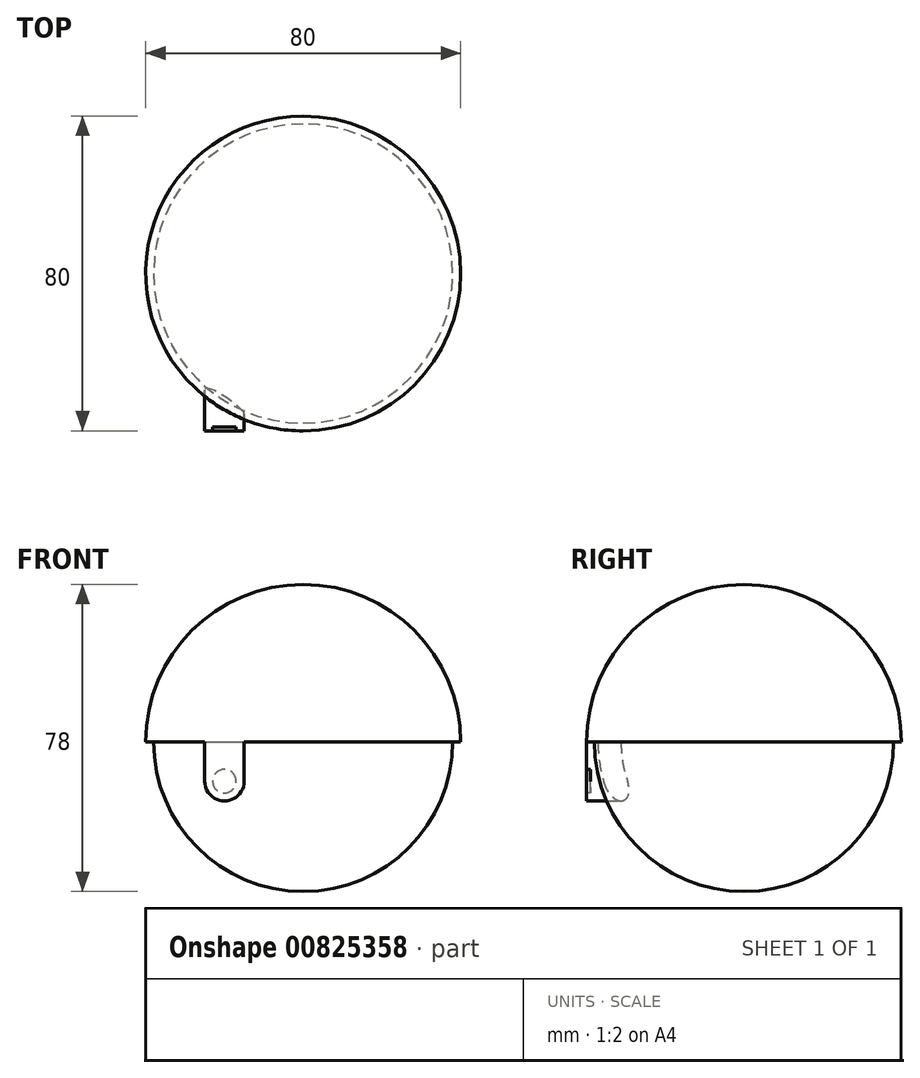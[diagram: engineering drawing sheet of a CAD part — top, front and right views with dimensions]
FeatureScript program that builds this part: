
annotation { "Feature Type Name" : "Feature", "Feature Type Description" : "" }
export const myFeature = defineFeature(function(context is Context, id is Id, definition is map)
    precondition{}
    {
        {
            var Q0;
            Q0=qCreatedBy(makeId("Top.planeOp"),FACE);
            var sketch = newSketch(context, id + "F0", { "sketchPlane" : qUnion([Q0])});
            skArc(sketch, "E0", {"start": v(0, 40) * mm, "mid": v(-40, 0) * mm, "end": v(0, -40) * mm});
            skLineSegment(sketch, "E1", {"start": v(0, 40) * mm, "end": v(0, -40) * mm});
            skSolve(sketch);
        }
        {
            var Q0;
            Q0=makeQuery(id+"F0.imprint","IMPRINT",FACE,{"disambiguationData":[TD([[makeQuery(id+"F0.imprint","IMPRINT",EDGE,{"derivedFrom":sQuery(id+"F0.wireOp",EDGE,"E0")}),1.0]])]});
            var Q1;
            Q1=sQuery(id+"F0.wireOp",EDGE,"E1");
            revolve(context, id + "F1", {"surfaceOperationType" : NewSurfaceOperationType.NEW, "entities" : qUnion([Q0]), "axis" : qUnion([Q1]), "revolveType" : RevolveType.ONE_DIRECTION, "angle" : 180 * degree});
        }
        {
            var Q0;
            Q0=qCreatedBy(makeId("Front.planeOp"),FACE);
            var sketch = newSketch(context, id + "F2", { "sketchPlane" : qUnion([Q0])});
            skArc(sketch, "E2", {"start": v(-25, -10) * mm, "mid": v(-20, -15) * mm, "end": v(-15, -10) * mm});
            skPoint(sketch, "E3.bottom.end.orphan", {"position": v(-15, -5) * mm});
            skPoint(sketch, "E3.bottom.start.orphan", {"position": v(-25, 0) * mm});
            skLineSegment(sketch, "E4", {"start": v(-25, -10) * mm, "end": v(-25, 0) * mm});
            skLineSegment(sketch, "E5", {"start": v(-15, -10) * mm, "end": v(-15, 0) * mm});
            skLineSegment(sketch, "E6", {"start": v(-25, 0) * mm, "end": v(-15, 0) * mm});
            skSolve(sketch);
        }
        {
            var Q0;
            Q0 = qSketchRegion(id + "F2", true);
            extrude(context, id + "F3", {"entities" : qUnion([Q0]), "operationType" : NewBodyOperationType.ADD, "depth" : 40 * mm, "offsetDistance" : 25 * mm});
        }
        {
            var Q0;
            Q0=makeQuery(id+"F3.opExtrude","CAP_FACE",FACE,{"disambiguationData":[OSD([sQuery(id+"F2.wireOp",EDGE,"E2"),sQuery(id+"F2.wireOp",EDGE,"E4"),sQuery(id+"F2.wireOp",EDGE,"E5"),sQuery(id+"F2.wireOp",EDGE,"E6")])],"isStart":false});
            var sketch = newSketch(context, id + "F4", { "sketchPlane" : qUnion([Q0])});
            skCircle(sketch, "E7", {"center": v(-20, -10) * mm, "radius": 3 * mm});
            skSolve(sketch);
        }
        {
            var Q0;
            Q0=makeQuery(id+"F4.imprint","IMPRINT",FACE,{"disambiguationData":[TD([[makeQuery(id+"F4.imprint","IMPRINT",EDGE,{"derivedFrom":sQuery(id+"F4.wireOp",EDGE,"E7")}),1.0]])]});
            extrude(context, id + "F5", {"entities" : qUnion([Q0]), "operationType" : NewBodyOperationType.REMOVE, "oppositeDirection" : true, "depth" : 1 * mm, "offsetDistance" : 25 * mm});
        }
        {
            var Q0;
            {var subQ0=sQuery(id+"F2.wireOp",EDGE,"E6");Q0=makeQuery(id+"FfjeHvJ9xTNGz3V_1.1.F3.boolean.opBoolean","MERGE",FACE,{"derivedFrom":[makeQuery(id+"F3.boolean.opBoolean","MERGE",FACE,{"derivedFrom":[makeQuery(id+"F1.opRevolve","CAP_FACE",FACE,{"disambiguationData":[OSD([sQuery(id+"F0.wireOp",EDGE,"E0"),sQuery(id+"F0.wireOp",EDGE,"E1")])],"isStart":true}),makeQuery(id+"F3.opExtrude","SWEPT_FACE",FACE,{"disambiguationData":[OSD([subQ0])]})]}),makeQuery(id+"FfjeHvJ9xTNGz3V_1.1.F3.opExtrude","SWEPT_FACE",FACE,{"disambiguationData":[OSD([subQ0])]})]});}
            var sketch = newSketch(context, id + "F6", { "sketchPlane" : qUnion([Q0])});
            skArc(sketch, "E8", {"start": v(0, -38) * mm, "mid": v(38, 0) * mm, "end": v(0, 38) * mm});
            skLineSegment(sketch, "E9", {"start": v(0, 38) * mm, "end": v(0, -38) * mm});
            skPoint(sketch, "E9.startSnap0", {"position": v(0, -40) * mm});
            skSolve(sketch);
        }
        {
            var Q0;
            Q0=makeQuery(id+"F6.imprint","IMPRINT",FACE,{"disambiguationData":[TD([[makeQuery(id+"F6.imprint","IMPRINT",EDGE,{"derivedFrom":sQuery(id+"F6.wireOp",EDGE,"E8")}),1.0]])]});
            var Q1;
            Q1=sQuery(id+"F6.wireOp",EDGE,"E9");
            revolve(context, id + "F7", {"operationType" : NewBodyOperationType.REMOVE, "surfaceOperationType" : NewSurfaceOperationType.NEW, "entities" : qUnion([Q0]), "axis" : qUnion([Q1]), "revolveType" : RevolveType.ONE_DIRECTION, "oppositeDirection" : true, "angle" : 180 * degree});
        }
    });
